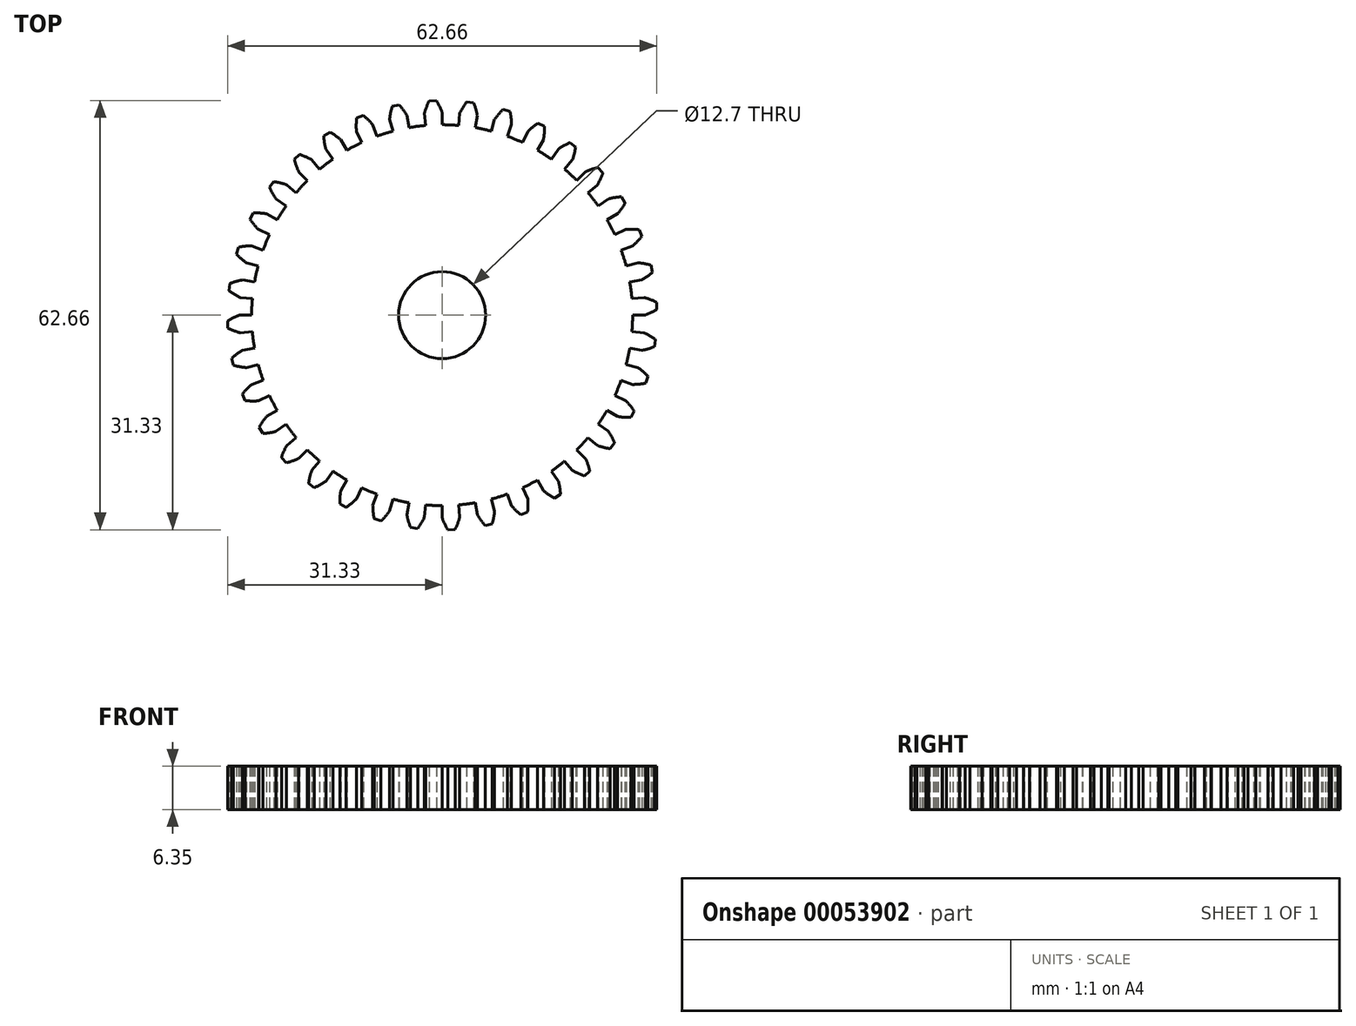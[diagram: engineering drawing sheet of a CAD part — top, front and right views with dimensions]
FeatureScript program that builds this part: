
annotation { "Feature Type Name" : "Feature", "Feature Type Description" : "" }
export const myFeature = defineFeature(function(context is Context, id is Id, definition is map)
    precondition{}
    {
        {
            var Q0;
            Q0=qCreatedBy(makeId("Top.planeOp"),FACE);
            var sketch = newSketch(context, id + "F0", { "sketchPlane" : qUnion([Q0])});
            skArc(sketch, "E0.trimOffspring", {"start": v(0, 29.59) * mm, "mid": v(-0.38, 30.48) * mm, "end": v(-0.85, 31.33) * mm});
            skPoint(sketch, "E1.start.orphan", {"position": v(0, 29.59) * mm});
            skLineSegment(sketch, "E2", {"start": v(0, 29.59) * mm, "end": v(0, 27.8) * mm});
            skLineSegment(sketch, "E3", {"start": v(-0.85, 31.33) * mm, "end": v(-1.37, 31.3) * mm});
            skPoint(sketch, "E3.endSnap0", {"position": v(-1.37, 31.31) * mm});
            skLineSegment(sketch, "E4.MirrorCS", {"start": v(-1.89, 31.28) * mm, "end": v(-1.37, 31.3) * mm});
            skArc(sketch, "E5.MirrorCS", {"start": v(-2.58, 29.47) * mm, "mid": v(-2.28, 30.4) * mm, "end": v(-1.89, 31.28) * mm});
            skLineSegment(sketch, "E6.MirrorCS", {"start": v(-2.58, 29.47) * mm, "end": v(-2.42, 27.7) * mm});
            skArc(sketch, "E7.1.0", {"start": v(-7.66, 28.58) * mm, "mid": v(-7.52, 29.54) * mm, "end": v(-7.3, 30.48) * mm});
            skLineSegment(sketch, "E7.1.1", {"start": v(-7.66, 28.58) * mm, "end": v(-7.2, 26.85) * mm});
            skLineSegment(sketch, "E7.1.2", {"start": v(-5.14, 29.14) * mm, "end": v(-4.83, 27.38) * mm});
            skArc(sketch, "E7.1.3", {"start": v(-5.14, 29.14) * mm, "mid": v(-5.67, 29.95) * mm, "end": v(-6.27, 30.7) * mm});
            skLineSegment(sketch, "E7.1.4", {"start": v(-6.27, 30.7) * mm, "end": v(-6.78, 30.6) * mm});
            skLineSegment(sketch, "E7.1.5", {"start": v(-7.3, 30.48) * mm, "end": v(-6.78, 30.6) * mm});
            skArc(sketch, "E7.2.0", {"start": v(-12.5, 26.81) * mm, "mid": v(-12.54, 27.78) * mm, "end": v(-12.47, 28.75) * mm});
            skLineSegment(sketch, "E7.2.1", {"start": v(-12.5, 26.81) * mm, "end": v(-11.75, 25.2) * mm});
            skLineSegment(sketch, "E7.2.2", {"start": v(-10.12, 27.8) * mm, "end": v(-9.5, 26.12) * mm});
            skArc(sketch, "E7.2.3", {"start": v(-10.12, 27.8) * mm, "mid": v(-10.78, 28.51) * mm, "end": v(-11.51, 29.15) * mm});
            skLineSegment(sketch, "E7.2.4", {"start": v(-11.51, 29.15) * mm, "end": v(-12, 28.95) * mm});
            skLineSegment(sketch, "E7.2.5", {"start": v(-12.47, 28.75) * mm, "end": v(-12, 28.95) * mm});
            skPoint(sketch, "E7.center", {"position": v(0, 0) * mm});
            skArc(sketch, "E8.2.3.0", {"start": v(-16.97, 24.23) * mm, "mid": v(-17.17, 25.18) * mm, "end": v(-17.28, 26.15) * mm});
            skLineSegment(sketch, "E8.4.3.0", {"start": v(-16.97, 24.23) * mm, "end": v(-15.95, 22.77) * mm});
            skLineSegment(sketch, "E8.7.3.0", {"start": v(-14.8, 25.62) * mm, "end": v(-13.9, 24.08) * mm});
            skArc(sketch, "E8.10.3.0", {"start": v(-14.8, 25.62) * mm, "mid": v(-15.57, 26.2) * mm, "end": v(-16.4, 26.7) * mm});
            skLineSegment(sketch, "E8.14.3.0", {"start": v(-16.4, 26.7) * mm, "end": v(-16.84, 26.43) * mm});
            skLineSegment(sketch, "E8.17.3.0", {"start": v(-17.28, 26.15) * mm, "end": v(-16.84, 26.43) * mm});
            skArc(sketch, "E8.2.4.0", {"start": v(-20.92, 20.92) * mm, "mid": v(-21.28, 21.82) * mm, "end": v(-21.55, 22.75) * mm});
            skLineSegment(sketch, "E8.4.4.0", {"start": v(-20.92, 20.92) * mm, "end": v(-19.66, 19.66) * mm});
            skLineSegment(sketch, "E8.7.4.0", {"start": v(-19.02, 22.66) * mm, "end": v(-17.87, 21.3) * mm});
            skArc(sketch, "E8.10.4.0", {"start": v(-19.02, 22.66) * mm, "mid": v(-19.88, 23.1) * mm, "end": v(-20.79, 23.46) * mm});
            skLineSegment(sketch, "E8.14.4.0", {"start": v(-20.79, 23.46) * mm, "end": v(-21.17, 23.1) * mm});
            skLineSegment(sketch, "E8.17.4.0", {"start": v(-21.55, 22.75) * mm, "end": v(-21.17, 23.1) * mm});
            skArc(sketch, "E8.2.5.0", {"start": v(-24.23, 16.97) * mm, "mid": v(-24.75, 17.8) * mm, "end": v(-25.18, 18.66) * mm});
            skLineSegment(sketch, "E8.4.5.0", {"start": v(-24.23, 16.97) * mm, "end": v(-22.77, 15.95) * mm});
            skLineSegment(sketch, "E8.7.5.0", {"start": v(-22.66, 19.02) * mm, "end": v(-21.3, 17.87) * mm});
            skArc(sketch, "E8.10.5.0", {"start": v(-22.66, 19.02) * mm, "mid": v(-23.6, 19.3) * mm, "end": v(-24.54, 19.49) * mm});
            skLineSegment(sketch, "E8.14.5.0", {"start": v(-24.54, 19.49) * mm, "end": v(-24.86, 19.08) * mm});
            skLineSegment(sketch, "E8.17.5.0", {"start": v(-25.18, 18.66) * mm, "end": v(-24.86, 19.08) * mm});
            skArc(sketch, "E8.2.6.0", {"start": v(-26.81, 12.5) * mm, "mid": v(-27.46, 13.22) * mm, "end": v(-28.04, 14) * mm});
            skLineSegment(sketch, "E8.4.6.0", {"start": v(-26.81, 12.5) * mm, "end": v(-25.2, 11.75) * mm});
            skLineSegment(sketch, "E8.7.6.0", {"start": v(-25.62, 14.8) * mm, "end": v(-24.08, 13.9) * mm});
            skArc(sketch, "E8.10.6.0", {"start": v(-25.62, 14.8) * mm, "mid": v(-26.58, 14.91) * mm, "end": v(-27.55, 14.93) * mm});
            skLineSegment(sketch, "E8.14.6.0", {"start": v(-27.55, 14.93) * mm, "end": v(-27.8, 14.47) * mm});
            skLineSegment(sketch, "E8.17.6.0", {"start": v(-28.04, 14) * mm, "end": v(-27.8, 14.47) * mm});
            skArc(sketch, "E8.2.7.0", {"start": v(-28.58, 7.66) * mm, "mid": v(-29.34, 8.25) * mm, "end": v(-30.04, 8.93) * mm});
            skLineSegment(sketch, "E8.4.7.0", {"start": v(-28.58, 7.66) * mm, "end": v(-26.85, 7.2) * mm});
            skLineSegment(sketch, "E8.7.7.0", {"start": v(-27.8, 10.12) * mm, "end": v(-26.12, 9.5) * mm});
            skArc(sketch, "E8.10.7.0", {"start": v(-27.8, 10.12) * mm, "mid": v(-28.77, 10.07) * mm, "end": v(-29.73, 9.92) * mm});
            skLineSegment(sketch, "E8.14.7.0", {"start": v(-29.73, 9.92) * mm, "end": v(-29.89, 9.42) * mm});
            skLineSegment(sketch, "E8.17.7.0", {"start": v(-30.04, 8.93) * mm, "end": v(-29.89, 9.42) * mm});
            skArc(sketch, "E8.2.8.0", {"start": v(-29.47, 2.58) * mm, "mid": v(-30.33, 3.03) * mm, "end": v(-31.14, 3.57) * mm});
            skLineSegment(sketch, "E8.4.8.0", {"start": v(-29.47, 2.58) * mm, "end": v(-27.7, 2.42) * mm});
            skLineSegment(sketch, "E8.7.8.0", {"start": v(-29.14, 5.14) * mm, "end": v(-27.38, 4.83) * mm});
            skArc(sketch, "E8.10.8.0", {"start": v(-29.14, 5.14) * mm, "mid": v(-30.08, 4.92) * mm, "end": v(-31, 4.6) * mm});
            skLineSegment(sketch, "E8.14.8.0", {"start": v(-31, 4.6) * mm, "end": v(-31.07, 4.09) * mm});
            skLineSegment(sketch, "E8.17.8.0", {"start": v(-31.14, 3.57) * mm, "end": v(-31.07, 4.1) * mm});
            skArc(sketch, "E8.2.9.0", {"start": v(-29.47, -2.58) * mm, "mid": v(-30.4, -2.28) * mm, "end": v(-31.28, -1.89) * mm});
            skLineSegment(sketch, "E8.4.9.0", {"start": v(-29.47, -2.58) * mm, "end": v(-27.7, -2.42) * mm});
            skLineSegment(sketch, "E8.7.9.0", {"start": v(-29.59, 0) * mm, "end": v(-27.8, 0) * mm});
            skArc(sketch, "E8.10.9.0", {"start": v(-29.59, 0) * mm, "mid": v(-30.48, -0.38) * mm, "end": v(-31.33, -0.85) * mm});
            skLineSegment(sketch, "E8.14.9.0", {"start": v(-31.33, -0.85) * mm, "end": v(-31.3, -1.37) * mm});
            skLineSegment(sketch, "E8.17.9.0", {"start": v(-31.28, -1.89) * mm, "end": v(-31.3, -1.37) * mm});
            skArc(sketch, "E8.2.10.0", {"start": v(-28.58, -7.66) * mm, "mid": v(-29.54, -7.52) * mm, "end": v(-30.48, -7.3) * mm});
            skLineSegment(sketch, "E8.4.10.0", {"start": v(-28.58, -7.66) * mm, "end": v(-26.85, -7.2) * mm});
            skLineSegment(sketch, "E8.7.10.0", {"start": v(-29.14, -5.14) * mm, "end": v(-27.38, -4.83) * mm});
            skArc(sketch, "E8.10.10.0", {"start": v(-29.14, -5.14) * mm, "mid": v(-29.95, -5.67) * mm, "end": v(-30.7, -6.27) * mm});
            skLineSegment(sketch, "E8.14.10.0", {"start": v(-30.7, -6.27) * mm, "end": v(-30.6, -6.78) * mm});
            skLineSegment(sketch, "E8.17.10.0", {"start": v(-30.48, -7.3) * mm, "end": v(-30.6, -6.78) * mm});
            skArc(sketch, "E8.2.11.0", {"start": v(-26.81, -12.5) * mm, "mid": v(-27.78, -12.54) * mm, "end": v(-28.75, -12.47) * mm});
            skLineSegment(sketch, "E8.4.11.0", {"start": v(-26.81, -12.5) * mm, "end": v(-25.2, -11.75) * mm});
            skLineSegment(sketch, "E8.7.11.0", {"start": v(-27.8, -10.12) * mm, "end": v(-26.12, -9.5) * mm});
            skArc(sketch, "E8.10.11.0", {"start": v(-27.8, -10.12) * mm, "mid": v(-28.51, -10.78) * mm, "end": v(-29.15, -11.51) * mm});
            skLineSegment(sketch, "E8.14.11.0", {"start": v(-29.15, -11.51) * mm, "end": v(-28.95, -12) * mm});
            skLineSegment(sketch, "E8.17.11.0", {"start": v(-28.75, -12.47) * mm, "end": v(-28.95, -12) * mm});
            skArc(sketch, "E8.2.12.0", {"start": v(-24.23, -16.97) * mm, "mid": v(-25.18, -17.17) * mm, "end": v(-26.15, -17.28) * mm});
            skLineSegment(sketch, "E8.4.12.0", {"start": v(-24.23, -16.97) * mm, "end": v(-22.77, -15.95) * mm});
            skLineSegment(sketch, "E8.7.12.0", {"start": v(-25.62, -14.8) * mm, "end": v(-24.08, -13.9) * mm});
            skArc(sketch, "E8.10.12.0", {"start": v(-25.62, -14.8) * mm, "mid": v(-26.2, -15.57) * mm, "end": v(-26.7, -16.4) * mm});
            skLineSegment(sketch, "E8.14.12.0", {"start": v(-26.7, -16.4) * mm, "end": v(-26.43, -16.84) * mm});
            skLineSegment(sketch, "E8.17.12.0", {"start": v(-26.15, -17.28) * mm, "end": v(-26.43, -16.84) * mm});
            skArc(sketch, "E8.2.13.0", {"start": v(-20.92, -20.92) * mm, "mid": v(-21.82, -21.28) * mm, "end": v(-22.75, -21.55) * mm});
            skLineSegment(sketch, "E8.4.13.0", {"start": v(-20.92, -20.92) * mm, "end": v(-19.66, -19.66) * mm});
            skLineSegment(sketch, "E8.7.13.0", {"start": v(-22.66, -19.02) * mm, "end": v(-21.3, -17.87) * mm});
            skArc(sketch, "E8.10.13.0", {"start": v(-22.66, -19.02) * mm, "mid": v(-23.1, -19.88) * mm, "end": v(-23.46, -20.79) * mm});
            skLineSegment(sketch, "E8.14.13.0", {"start": v(-23.46, -20.79) * mm, "end": v(-23.1, -21.17) * mm});
            skLineSegment(sketch, "E8.17.13.0", {"start": v(-22.75, -21.55) * mm, "end": v(-23.1, -21.17) * mm});
            skArc(sketch, "E8.2.14.0", {"start": v(-16.97, -24.23) * mm, "mid": v(-17.8, -24.75) * mm, "end": v(-18.66, -25.18) * mm});
            skLineSegment(sketch, "E8.4.14.0", {"start": v(-16.97, -24.23) * mm, "end": v(-15.95, -22.77) * mm});
            skLineSegment(sketch, "E8.7.14.0", {"start": v(-19.02, -22.66) * mm, "end": v(-17.87, -21.3) * mm});
            skArc(sketch, "E8.10.14.0", {"start": v(-19.02, -22.66) * mm, "mid": v(-19.3, -23.6) * mm, "end": v(-19.49, -24.54) * mm});
            skLineSegment(sketch, "E8.14.14.0", {"start": v(-19.49, -24.54) * mm, "end": v(-19.08, -24.86) * mm});
            skLineSegment(sketch, "E8.17.14.0", {"start": v(-18.66, -25.18) * mm, "end": v(-19.08, -24.86) * mm});
            skArc(sketch, "E8.2.15.0", {"start": v(-12.5, -26.81) * mm, "mid": v(-13.22, -27.46) * mm, "end": v(-14, -28.04) * mm});
            skLineSegment(sketch, "E8.4.15.0", {"start": v(-12.5, -26.81) * mm, "end": v(-11.75, -25.2) * mm});
            skLineSegment(sketch, "E8.7.15.0", {"start": v(-14.8, -25.62) * mm, "end": v(-13.9, -24.08) * mm});
            skArc(sketch, "E8.10.15.0", {"start": v(-14.8, -25.62) * mm, "mid": v(-14.91, -26.58) * mm, "end": v(-14.93, -27.55) * mm});
            skLineSegment(sketch, "E8.14.15.0", {"start": v(-14.93, -27.55) * mm, "end": v(-14.47, -27.8) * mm});
            skLineSegment(sketch, "E8.17.15.0", {"start": v(-14, -28.04) * mm, "end": v(-14.47, -27.8) * mm});
            skArc(sketch, "E8.2.16.0", {"start": v(-7.66, -28.58) * mm, "mid": v(-8.25, -29.34) * mm, "end": v(-8.93, -30.04) * mm});
            skLineSegment(sketch, "E8.4.16.0", {"start": v(-7.66, -28.58) * mm, "end": v(-7.2, -26.85) * mm});
            skLineSegment(sketch, "E8.7.16.0", {"start": v(-10.12, -27.8) * mm, "end": v(-9.5, -26.12) * mm});
            skArc(sketch, "E8.10.16.0", {"start": v(-10.12, -27.8) * mm, "mid": v(-10.07, -28.77) * mm, "end": v(-9.92, -29.73) * mm});
            skLineSegment(sketch, "E8.14.16.0", {"start": v(-9.92, -29.73) * mm, "end": v(-9.42, -29.89) * mm});
            skLineSegment(sketch, "E8.17.16.0", {"start": v(-8.93, -30.04) * mm, "end": v(-9.42, -29.89) * mm});
            skArc(sketch, "E8.2.17.0", {"start": v(-2.58, -29.47) * mm, "mid": v(-3.03, -30.33) * mm, "end": v(-3.57, -31.14) * mm});
            skLineSegment(sketch, "E8.4.17.0", {"start": v(-2.58, -29.47) * mm, "end": v(-2.42, -27.7) * mm});
            skLineSegment(sketch, "E8.7.17.0", {"start": v(-5.14, -29.14) * mm, "end": v(-4.83, -27.38) * mm});
            skArc(sketch, "E8.10.17.0", {"start": v(-5.14, -29.14) * mm, "mid": v(-4.92, -30.08) * mm, "end": v(-4.6, -31) * mm});
            skLineSegment(sketch, "E8.14.17.0", {"start": v(-4.6, -31) * mm, "end": v(-4.09, -31.07) * mm});
            skLineSegment(sketch, "E8.17.17.0", {"start": v(-3.57, -31.14) * mm, "end": v(-4.1, -31.07) * mm});
            skArc(sketch, "E8.2.18.0", {"start": v(2.58, -29.47) * mm, "mid": v(2.28, -30.4) * mm, "end": v(1.89, -31.28) * mm});
            skLineSegment(sketch, "E8.4.18.0", {"start": v(2.58, -29.47) * mm, "end": v(2.42, -27.7) * mm});
            skLineSegment(sketch, "E8.7.18.0", {"start": v(0, -29.59) * mm, "end": v(0, -27.8) * mm});
            skArc(sketch, "E8.10.18.0", {"start": v(0, -29.59) * mm, "mid": v(0.38, -30.48) * mm, "end": v(0.85, -31.33) * mm});
            skLineSegment(sketch, "E8.14.18.0", {"start": v(0.85, -31.33) * mm, "end": v(1.37, -31.3) * mm});
            skLineSegment(sketch, "E8.17.18.0", {"start": v(1.89, -31.28) * mm, "end": v(1.37, -31.3) * mm});
            skArc(sketch, "E8.2.19.0", {"start": v(7.66, -28.58) * mm, "mid": v(7.52, -29.54) * mm, "end": v(7.3, -30.48) * mm});
            skLineSegment(sketch, "E8.4.19.0", {"start": v(7.66, -28.58) * mm, "end": v(7.2, -26.85) * mm});
            skLineSegment(sketch, "E8.7.19.0", {"start": v(5.14, -29.14) * mm, "end": v(4.83, -27.38) * mm});
            skArc(sketch, "E8.10.19.0", {"start": v(5.14, -29.14) * mm, "mid": v(5.67, -29.95) * mm, "end": v(6.27, -30.7) * mm});
            skLineSegment(sketch, "E8.14.19.0", {"start": v(6.27, -30.7) * mm, "end": v(6.78, -30.6) * mm});
            skLineSegment(sketch, "E8.17.19.0", {"start": v(7.3, -30.48) * mm, "end": v(6.78, -30.6) * mm});
            skArc(sketch, "E8.2.20.0", {"start": v(12.5, -26.81) * mm, "mid": v(12.54, -27.78) * mm, "end": v(12.47, -28.75) * mm});
            skLineSegment(sketch, "E8.4.20.0", {"start": v(12.5, -26.81) * mm, "end": v(11.75, -25.2) * mm});
            skLineSegment(sketch, "E8.7.20.0", {"start": v(10.12, -27.8) * mm, "end": v(9.5, -26.12) * mm});
            skArc(sketch, "E8.10.20.0", {"start": v(10.12, -27.8) * mm, "mid": v(10.78, -28.51) * mm, "end": v(11.51, -29.15) * mm});
            skLineSegment(sketch, "E8.14.20.0", {"start": v(11.51, -29.15) * mm, "end": v(12, -28.95) * mm});
            skLineSegment(sketch, "E8.17.20.0", {"start": v(12.47, -28.75) * mm, "end": v(12, -28.95) * mm});
            skArc(sketch, "E8.2.21.0", {"start": v(16.97, -24.23) * mm, "mid": v(17.17, -25.18) * mm, "end": v(17.28, -26.15) * mm});
            skLineSegment(sketch, "E8.4.21.0", {"start": v(16.97, -24.23) * mm, "end": v(15.95, -22.77) * mm});
            skLineSegment(sketch, "E8.7.21.0", {"start": v(14.8, -25.62) * mm, "end": v(13.9, -24.08) * mm});
            skArc(sketch, "E8.10.21.0", {"start": v(14.8, -25.62) * mm, "mid": v(15.57, -26.2) * mm, "end": v(16.4, -26.7) * mm});
            skLineSegment(sketch, "E8.14.21.0", {"start": v(16.4, -26.7) * mm, "end": v(16.84, -26.43) * mm});
            skLineSegment(sketch, "E8.17.21.0", {"start": v(17.28, -26.15) * mm, "end": v(16.84, -26.43) * mm});
            skArc(sketch, "E8.2.22.0", {"start": v(20.92, -20.92) * mm, "mid": v(21.28, -21.82) * mm, "end": v(21.55, -22.75) * mm});
            skLineSegment(sketch, "E8.4.22.0", {"start": v(20.92, -20.92) * mm, "end": v(19.66, -19.66) * mm});
            skLineSegment(sketch, "E8.7.22.0", {"start": v(19.02, -22.66) * mm, "end": v(17.87, -21.3) * mm});
            skArc(sketch, "E8.10.22.0", {"start": v(19.02, -22.66) * mm, "mid": v(19.88, -23.1) * mm, "end": v(20.79, -23.46) * mm});
            skLineSegment(sketch, "E8.14.22.0", {"start": v(20.79, -23.46) * mm, "end": v(21.17, -23.1) * mm});
            skLineSegment(sketch, "E8.17.22.0", {"start": v(21.55, -22.75) * mm, "end": v(21.17, -23.1) * mm});
            skArc(sketch, "E8.2.23.0", {"start": v(24.23, -16.97) * mm, "mid": v(24.75, -17.8) * mm, "end": v(25.18, -18.66) * mm});
            skLineSegment(sketch, "E8.4.23.0", {"start": v(24.23, -16.97) * mm, "end": v(22.77, -15.95) * mm});
            skLineSegment(sketch, "E8.7.23.0", {"start": v(22.66, -19.02) * mm, "end": v(21.3, -17.87) * mm});
            skArc(sketch, "E8.10.23.0", {"start": v(22.66, -19.02) * mm, "mid": v(23.6, -19.3) * mm, "end": v(24.54, -19.49) * mm});
            skLineSegment(sketch, "E8.14.23.0", {"start": v(24.54, -19.49) * mm, "end": v(24.86, -19.08) * mm});
            skLineSegment(sketch, "E8.17.23.0", {"start": v(25.18, -18.66) * mm, "end": v(24.86, -19.08) * mm});
            skArc(sketch, "E8.2.24.0", {"start": v(26.81, -12.5) * mm, "mid": v(27.46, -13.22) * mm, "end": v(28.04, -14) * mm});
            skLineSegment(sketch, "E8.4.24.0", {"start": v(26.81, -12.5) * mm, "end": v(25.2, -11.75) * mm});
            skLineSegment(sketch, "E8.7.24.0", {"start": v(25.62, -14.8) * mm, "end": v(24.08, -13.9) * mm});
            skArc(sketch, "E8.10.24.0", {"start": v(25.62, -14.8) * mm, "mid": v(26.58, -14.91) * mm, "end": v(27.55, -14.93) * mm});
            skLineSegment(sketch, "E8.14.24.0", {"start": v(27.55, -14.93) * mm, "end": v(27.8, -14.47) * mm});
            skLineSegment(sketch, "E8.17.24.0", {"start": v(28.04, -14) * mm, "end": v(27.8, -14.47) * mm});
            skArc(sketch, "E8.2.25.0", {"start": v(28.58, -7.66) * mm, "mid": v(29.34, -8.25) * mm, "end": v(30.04, -8.93) * mm});
            skLineSegment(sketch, "E8.4.25.0", {"start": v(28.58, -7.66) * mm, "end": v(26.85, -7.2) * mm});
            skLineSegment(sketch, "E8.7.25.0", {"start": v(27.8, -10.12) * mm, "end": v(26.12, -9.5) * mm});
            skArc(sketch, "E8.10.25.0", {"start": v(27.8, -10.12) * mm, "mid": v(28.77, -10.07) * mm, "end": v(29.73, -9.92) * mm});
            skLineSegment(sketch, "E8.14.25.0", {"start": v(29.73, -9.92) * mm, "end": v(29.89, -9.42) * mm});
            skLineSegment(sketch, "E8.17.25.0", {"start": v(30.04, -8.93) * mm, "end": v(29.89, -9.42) * mm});
            skArc(sketch, "E8.2.26.0", {"start": v(29.47, -2.58) * mm, "mid": v(30.33, -3.03) * mm, "end": v(31.14, -3.57) * mm});
            skLineSegment(sketch, "E8.4.26.0", {"start": v(29.47, -2.58) * mm, "end": v(27.7, -2.42) * mm});
            skLineSegment(sketch, "E8.7.26.0", {"start": v(29.14, -5.14) * mm, "end": v(27.38, -4.83) * mm});
            skArc(sketch, "E8.10.26.0", {"start": v(29.14, -5.14) * mm, "mid": v(30.08, -4.92) * mm, "end": v(31, -4.6) * mm});
            skLineSegment(sketch, "E8.14.26.0", {"start": v(31, -4.6) * mm, "end": v(31.07, -4.09) * mm});
            skLineSegment(sketch, "E8.17.26.0", {"start": v(31.14, -3.57) * mm, "end": v(31.07, -4.1) * mm});
            skArc(sketch, "E8.2.27.0", {"start": v(29.47, 2.58) * mm, "mid": v(30.4, 2.28) * mm, "end": v(31.28, 1.89) * mm});
            skLineSegment(sketch, "E8.4.27.0", {"start": v(29.47, 2.58) * mm, "end": v(27.7, 2.42) * mm});
            skLineSegment(sketch, "E8.7.27.0", {"start": v(29.59, 0) * mm, "end": v(27.8, 0) * mm});
            skArc(sketch, "E8.10.27.0", {"start": v(29.59, 0) * mm, "mid": v(30.48, 0.38) * mm, "end": v(31.33, 0.85) * mm});
            skLineSegment(sketch, "E8.14.27.0", {"start": v(31.33, 0.85) * mm, "end": v(31.3, 1.37) * mm});
            skLineSegment(sketch, "E8.17.27.0", {"start": v(31.28, 1.89) * mm, "end": v(31.3, 1.37) * mm});
            skArc(sketch, "E8.2.28.0", {"start": v(28.58, 7.66) * mm, "mid": v(29.54, 7.52) * mm, "end": v(30.48, 7.3) * mm});
            skLineSegment(sketch, "E8.4.28.0", {"start": v(28.58, 7.66) * mm, "end": v(26.85, 7.2) * mm});
            skLineSegment(sketch, "E8.7.28.0", {"start": v(29.14, 5.14) * mm, "end": v(27.38, 4.83) * mm});
            skArc(sketch, "E8.10.28.0", {"start": v(29.14, 5.14) * mm, "mid": v(29.95, 5.67) * mm, "end": v(30.7, 6.27) * mm});
            skLineSegment(sketch, "E8.14.28.0", {"start": v(30.7, 6.27) * mm, "end": v(30.6, 6.78) * mm});
            skLineSegment(sketch, "E8.17.28.0", {"start": v(30.48, 7.3) * mm, "end": v(30.6, 6.78) * mm});
            skArc(sketch, "E8.2.29.0", {"start": v(26.81, 12.5) * mm, "mid": v(27.78, 12.54) * mm, "end": v(28.75, 12.47) * mm});
            skLineSegment(sketch, "E8.4.29.0", {"start": v(26.81, 12.5) * mm, "end": v(25.2, 11.75) * mm});
            skLineSegment(sketch, "E8.7.29.0", {"start": v(27.8, 10.12) * mm, "end": v(26.12, 9.5) * mm});
            skArc(sketch, "E8.10.29.0", {"start": v(27.8, 10.12) * mm, "mid": v(28.51, 10.78) * mm, "end": v(29.15, 11.51) * mm});
            skLineSegment(sketch, "E8.14.29.0", {"start": v(29.15, 11.51) * mm, "end": v(28.95, 12) * mm});
            skLineSegment(sketch, "E8.17.29.0", {"start": v(28.75, 12.47) * mm, "end": v(28.95, 12) * mm});
            skArc(sketch, "E8.2.30.0", {"start": v(24.23, 16.97) * mm, "mid": v(25.18, 17.17) * mm, "end": v(26.15, 17.28) * mm});
            skLineSegment(sketch, "E8.4.30.0", {"start": v(24.23, 16.97) * mm, "end": v(22.77, 15.95) * mm});
            skLineSegment(sketch, "E8.7.30.0", {"start": v(25.62, 14.8) * mm, "end": v(24.08, 13.9) * mm});
            skArc(sketch, "E8.10.30.0", {"start": v(25.62, 14.8) * mm, "mid": v(26.2, 15.57) * mm, "end": v(26.7, 16.4) * mm});
            skLineSegment(sketch, "E8.14.30.0", {"start": v(26.7, 16.4) * mm, "end": v(26.43, 16.84) * mm});
            skLineSegment(sketch, "E8.17.30.0", {"start": v(26.15, 17.28) * mm, "end": v(26.43, 16.84) * mm});
            skArc(sketch, "E8.2.31.0", {"start": v(20.92, 20.92) * mm, "mid": v(21.82, 21.28) * mm, "end": v(22.75, 21.55) * mm});
            skLineSegment(sketch, "E8.4.31.0", {"start": v(20.92, 20.92) * mm, "end": v(19.66, 19.66) * mm});
            skLineSegment(sketch, "E8.7.31.0", {"start": v(22.66, 19.02) * mm, "end": v(21.3, 17.87) * mm});
            skArc(sketch, "E8.10.31.0", {"start": v(22.66, 19.02) * mm, "mid": v(23.1, 19.88) * mm, "end": v(23.46, 20.79) * mm});
            skLineSegment(sketch, "E8.14.31.0", {"start": v(23.46, 20.79) * mm, "end": v(23.1, 21.17) * mm});
            skLineSegment(sketch, "E8.17.31.0", {"start": v(22.75, 21.55) * mm, "end": v(23.1, 21.17) * mm});
            skArc(sketch, "E8.2.32.0", {"start": v(16.97, 24.23) * mm, "mid": v(17.8, 24.75) * mm, "end": v(18.66, 25.18) * mm});
            skLineSegment(sketch, "E8.4.32.0", {"start": v(16.97, 24.23) * mm, "end": v(15.95, 22.77) * mm});
            skLineSegment(sketch, "E8.7.32.0", {"start": v(19.02, 22.66) * mm, "end": v(17.87, 21.3) * mm});
            skArc(sketch, "E8.10.32.0", {"start": v(19.02, 22.66) * mm, "mid": v(19.3, 23.6) * mm, "end": v(19.49, 24.54) * mm});
            skLineSegment(sketch, "E8.14.32.0", {"start": v(19.49, 24.54) * mm, "end": v(19.08, 24.86) * mm});
            skLineSegment(sketch, "E8.17.32.0", {"start": v(18.66, 25.18) * mm, "end": v(19.08, 24.86) * mm});
            skArc(sketch, "E8.2.33.0", {"start": v(12.5, 26.81) * mm, "mid": v(13.22, 27.46) * mm, "end": v(14, 28.04) * mm});
            skLineSegment(sketch, "E8.4.33.0", {"start": v(12.5, 26.81) * mm, "end": v(11.75, 25.2) * mm});
            skLineSegment(sketch, "E8.7.33.0", {"start": v(14.8, 25.62) * mm, "end": v(13.9, 24.08) * mm});
            skArc(sketch, "E8.10.33.0", {"start": v(14.8, 25.62) * mm, "mid": v(14.91, 26.58) * mm, "end": v(14.93, 27.55) * mm});
            skLineSegment(sketch, "E8.14.33.0", {"start": v(14.93, 27.55) * mm, "end": v(14.47, 27.8) * mm});
            skLineSegment(sketch, "E8.17.33.0", {"start": v(14, 28.04) * mm, "end": v(14.47, 27.8) * mm});
            skArc(sketch, "E8.2.34.0", {"start": v(7.66, 28.58) * mm, "mid": v(8.25, 29.34) * mm, "end": v(8.93, 30.04) * mm});
            skLineSegment(sketch, "E8.4.34.0", {"start": v(7.66, 28.58) * mm, "end": v(7.2, 26.85) * mm});
            skLineSegment(sketch, "E8.7.34.0", {"start": v(10.12, 27.8) * mm, "end": v(9.5, 26.12) * mm});
            skArc(sketch, "E8.10.34.0", {"start": v(10.12, 27.8) * mm, "mid": v(10.07, 28.77) * mm, "end": v(9.92, 29.73) * mm});
            skLineSegment(sketch, "E8.14.34.0", {"start": v(9.92, 29.73) * mm, "end": v(9.42, 29.89) * mm});
            skLineSegment(sketch, "E8.17.34.0", {"start": v(8.93, 30.04) * mm, "end": v(9.42, 29.89) * mm});
            skArc(sketch, "E8.2.35.0", {"start": v(2.58, 29.47) * mm, "mid": v(3.03, 30.33) * mm, "end": v(3.57, 31.14) * mm});
            skLineSegment(sketch, "E8.4.35.0", {"start": v(2.58, 29.47) * mm, "end": v(2.42, 27.7) * mm});
            skLineSegment(sketch, "E8.7.35.0", {"start": v(5.14, 29.14) * mm, "end": v(4.83, 27.38) * mm});
            skArc(sketch, "E8.10.35.0", {"start": v(5.14, 29.14) * mm, "mid": v(4.92, 30.08) * mm, "end": v(4.6, 31) * mm});
            skLineSegment(sketch, "E8.14.35.0", {"start": v(4.6, 31) * mm, "end": v(4.09, 31.07) * mm});
            skLineSegment(sketch, "E8.17.35.0", {"start": v(3.57, 31.14) * mm, "end": v(4.1, 31.07) * mm});
            skLineSegment(sketch, "E9", {"start": v(-9.5, 26.12) * mm, "end": v(-7.2, 26.85) * mm});
            skArc(sketch, "E10", {"start": v(-11.75, 25.2) * mm, "mid": v(-12.84, 24.66) * mm, "end": v(-13.9, 24.08) * mm});
            skArc(sketch, "E11", {"start": v(-15.95, 22.77) * mm, "mid": v(-16.92, 22.06) * mm, "end": v(-17.87, 21.3) * mm});
            skArc(sketch, "E12", {"start": v(-19.66, 19.66) * mm, "mid": v(-20.5, 18.78) * mm, "end": v(-21.3, 17.87) * mm});
            skArc(sketch, "E13", {"start": v(-22.77, 15.95) * mm, "mid": v(-23.45, 14.94) * mm, "end": v(-24.08, 13.9) * mm});
            skArc(sketch, "E14", {"start": v(-25.2, 11.75) * mm, "mid": v(-25.68, 10.64) * mm, "end": v(-26.12, 9.5) * mm});
            skArc(sketch, "E15", {"start": v(-26.85, 7.2) * mm, "mid": v(-27.14, 6.02) * mm, "end": v(-27.38, 4.83) * mm});
            skArc(sketch, "E16", {"start": v(-27.7, 2.42) * mm, "mid": v(-27.77, 1.21) * mm, "end": v(-27.8, 0) * mm});
            skArc(sketch, "E17.trimOffspring", {"start": v(-7.2, 26.85) * mm, "mid": v(-8.36, 26.51) * mm, "end": v(-9.5, 26.12) * mm});
            skArc(sketch, "E18.trimOffspring", {"start": v(-2.42, 27.7) * mm, "mid": v(-3.63, 27.56) * mm, "end": v(-4.83, 27.38) * mm});
            skArc(sketch, "E19.trimOffspring", {"start": v(2.42, 27.7) * mm, "mid": v(1.21, 27.77) * mm, "end": v(0, 27.8) * mm});
            skArc(sketch, "E20.trimOffspring", {"start": v(7.2, 26.85) * mm, "mid": v(6.02, 27.14) * mm, "end": v(4.83, 27.38) * mm});
            skArc(sketch, "E21.trimOffspring", {"start": v(11.75, 25.2) * mm, "mid": v(10.64, 25.68) * mm, "end": v(9.5, 26.12) * mm});
            skArc(sketch, "E22.trimOffspring", {"start": v(15.95, 22.77) * mm, "mid": v(14.94, 23.45) * mm, "end": v(13.9, 24.08) * mm});
            skArc(sketch, "E23.trimOffspring", {"start": v(19.66, 19.66) * mm, "mid": v(18.78, 20.5) * mm, "end": v(17.87, 21.3) * mm});
            skArc(sketch, "E24.trimOffspring", {"start": v(22.77, 15.95) * mm, "mid": v(22.06, 16.92) * mm, "end": v(21.3, 17.87) * mm});
            skArc(sketch, "E25.trimOffspring", {"start": v(25.2, 11.75) * mm, "mid": v(24.66, 12.84) * mm, "end": v(24.08, 13.9) * mm});
            skArc(sketch, "E26.trimOffspring", {"start": v(-27.7, -2.42) * mm, "mid": v(-27.56, -3.63) * mm, "end": v(-27.38, -4.83) * mm});
            skArc(sketch, "E27.trimOffspring", {"start": v(-26.85, -7.2) * mm, "mid": v(-26.51, -8.36) * mm, "end": v(-26.12, -9.5) * mm});
            skArc(sketch, "E28.trimOffspring", {"start": v(-25.2, -11.75) * mm, "mid": v(-24.66, -12.84) * mm, "end": v(-24.08, -13.9) * mm});
            skArc(sketch, "E29.trimOffspring", {"start": v(-22.77, -15.95) * mm, "mid": v(-22.06, -16.92) * mm, "end": v(-21.3, -17.87) * mm});
            skArc(sketch, "E30.trimOffspring", {"start": v(26.85, 7.2) * mm, "mid": v(26.51, 8.36) * mm, "end": v(26.12, 9.5) * mm});
            skArc(sketch, "E31.trimOffspring", {"start": v(27.7, 2.42) * mm, "mid": v(27.56, 3.63) * mm, "end": v(27.38, 4.83) * mm});
            skArc(sketch, "E32.trimOffspring", {"start": v(27.7, -2.42) * mm, "mid": v(27.77, -1.21) * mm, "end": v(27.8, 0) * mm});
            skArc(sketch, "E33.trimOffspring", {"start": v(26.85, -7.2) * mm, "mid": v(27.14, -6.02) * mm, "end": v(27.38, -4.83) * mm});
            skArc(sketch, "E34.trimOffspring", {"start": v(25.2, -11.75) * mm, "mid": v(25.68, -10.64) * mm, "end": v(26.12, -9.5) * mm});
            skArc(sketch, "E35.trimOffspring", {"start": v(22.77, -15.95) * mm, "mid": v(23.45, -14.94) * mm, "end": v(24.08, -13.9) * mm});
            skArc(sketch, "E36.trimOffspring", {"start": v(19.66, -19.66) * mm, "mid": v(20.5, -18.78) * mm, "end": v(21.3, -17.87) * mm});
            skArc(sketch, "E37.trimOffspring", {"start": v(15.95, -22.77) * mm, "mid": v(16.92, -22.06) * mm, "end": v(17.87, -21.3) * mm});
            skArc(sketch, "E38.trimOffspring", {"start": v(11.75, -25.2) * mm, "mid": v(12.84, -24.66) * mm, "end": v(13.9, -24.08) * mm});
            skArc(sketch, "E39.trimOffspring", {"start": v(7.2, -26.85) * mm, "mid": v(8.36, -26.51) * mm, "end": v(9.5, -26.12) * mm});
            skArc(sketch, "E40.trimOffspring", {"start": v(2.42, -27.7) * mm, "mid": v(3.63, -27.56) * mm, "end": v(4.83, -27.38) * mm});
            skArc(sketch, "E41.trimOffspring", {"start": v(-2.42, -27.7) * mm, "mid": v(-1.21, -27.77) * mm, "end": v(0, -27.8) * mm});
            skArc(sketch, "E42.trimOffspring", {"start": v(-7.2, -26.85) * mm, "mid": v(-6.02, -27.14) * mm, "end": v(-4.83, -27.38) * mm});
            skArc(sketch, "E43.trimOffspring", {"start": v(-11.75, -25.2) * mm, "mid": v(-10.64, -25.68) * mm, "end": v(-9.5, -26.12) * mm});
            skArc(sketch, "E44.trimOffspring", {"start": v(-15.95, -22.77) * mm, "mid": v(-14.94, -23.45) * mm, "end": v(-13.9, -24.08) * mm});
            skArc(sketch, "E45.trimOffspring", {"start": v(-19.66, -19.66) * mm, "mid": v(-18.78, -20.5) * mm, "end": v(-17.87, -21.3) * mm});
            skCircle(sketch, "E46", {"center": v(0, 0) * mm, "radius": 6.35 * mm});
            skSolve(sketch);
        }
        {
            var Q0;
            Q0 = qSketchRegion(id + "F0", true);
            var Q1;
            Q1=makeQuery(id+"F0.imprint","IMPRINT",FACE,{"disambiguationData":[TD([[makeQuery(id+"F0.imprint","IMPRINT",EDGE,{"derivedFrom":sQuery(id+"F0.wireOp",EDGE,"E0.trimOffspring")}),1.0]])]});
            var Q2;
            Q2=makeQuery(id+"F0.imprint","IMPRINT",FACE,{"disambiguationData":[TD([[makeQuery(id+"F0.imprint","IMPRINT",EDGE,{"derivedFrom":sQuery(id+"F0.wireOp",EDGE,"E46")}),1.0]])]});
            extrude(context, id + "F1", {"entities" : qUnion([Q0, Q1, Q2]), "depth" : 6.35 * mm});
        }
        {
            var Q0;
            Q0=makeQuery(id+"F0.imprint","IMPRINT",FACE,{"disambiguationData":[TD([[makeQuery(id+"F0.imprint","IMPRINT",EDGE,{"derivedFrom":sQuery(id+"F0.wireOp",EDGE,"E46")}),1.0]])]});
            extrude(context, id + "F2", {"entities" : qUnion([Q0]), "operationType" : NewBodyOperationType.REMOVE, "depth" : 97.18 * mm});
        }
    });
